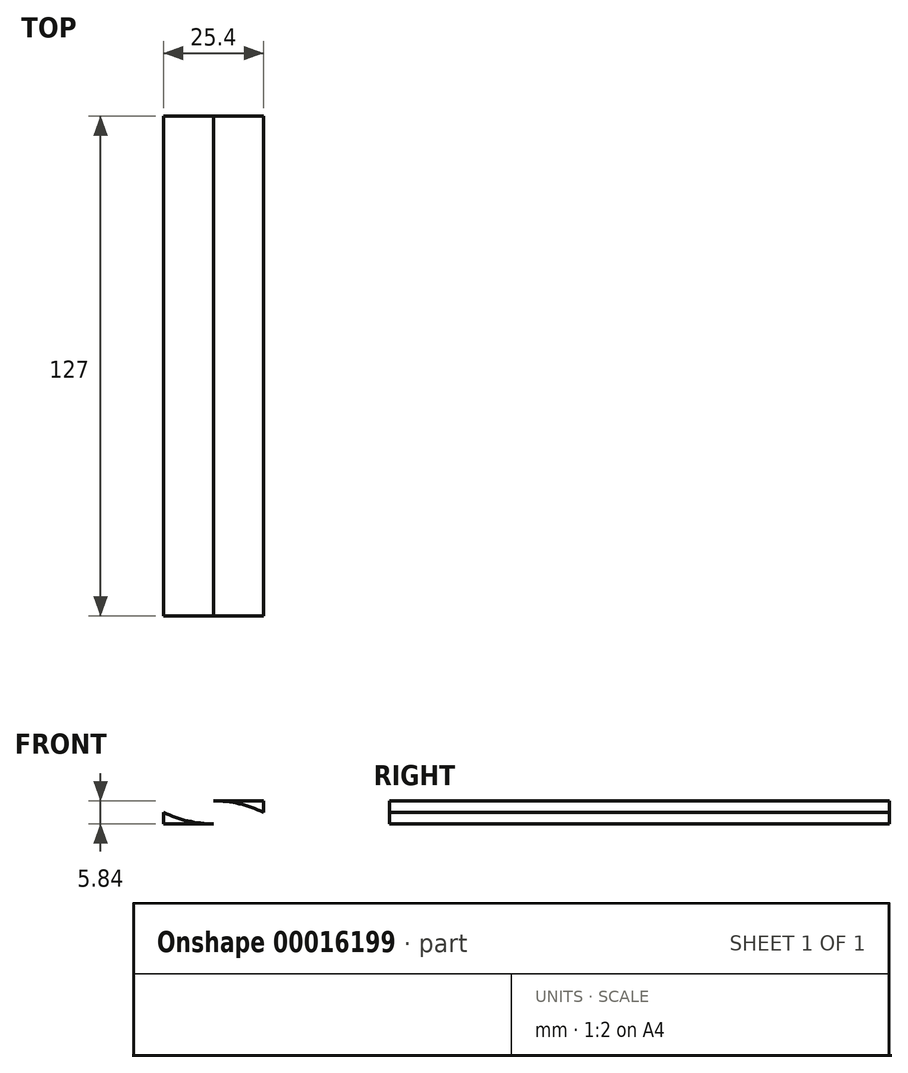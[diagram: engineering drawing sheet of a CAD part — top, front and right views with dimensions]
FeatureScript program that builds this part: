
annotation { "Feature Type Name" : "Feature", "Feature Type Description" : "" }
export const myFeature = defineFeature(function(context is Context, id is Id, definition is map)
    precondition{}
    {
        {
            var Q0;
            Q0=qCreatedBy(makeId("Top.planeOp"),FACE);
            var sketch = newSketch(context, id + "F0", { "sketchPlane" : qUnion([Q0])});
            skLineSegment(sketch, "E0.rect.bottom", {"start": v(-12.7, 63.5) * mm, "end": v(12.7, 63.5) * mm});
            skLineSegment(sketch, "E0.rect.top", {"start": v(-12.7, -63.5) * mm, "end": v(12.7, -63.5) * mm});
            skLineSegment(sketch, "E0.rect.left", {"start": v(-12.7, 63.5) * mm, "end": v(-12.7, -63.5) * mm});
            skLineSegment(sketch, "E0.rect.right", {"start": v(12.7, 63.5) * mm, "end": v(12.7, -63.5) * mm});
            skPoint(sketch, "E0.rect.middle", {"position": v(0, 0) * mm});
            skSolve(sketch);
        }
        {
            var Q0;
            Q0=makeQuery(id+"F0.imprint","IMPRINT",FACE,{"disambiguationData":[TD([[makeQuery(id+"F0.imprint","IMPRINT",EDGE,{"derivedFrom":sQuery(id+"F0.wireOp",EDGE,"E0.rect.bottom")}),-1.0]])]});
            extrude(context, id + "F1", {"entities" : qUnion([Q0]), "endBound" : BoundingType.SYMMETRIC, "depth" : 5.84 * mm});
        }
        {
            var Q0;
            Q0=makeQuery(id+"F1.opExtrude","SWEPT_FACE",FACE,{"disambiguationData":[OSD([sQuery(id+"F0.wireOp",EDGE,"E0.rect.top")])]});
            var sketch = newSketch(context, id + "F2", { "sketchPlane" : qUnion([Q0])});
            skArc(sketch, "E1", {"start": v(0, 2.92) * mm, "mid": v(-6.52, 2.18) * mm, "end": v(-12.7, 0) * mm});
            skLineSegment(sketch, "E2", {"start": v(-12.7, 0) * mm, "end": v(12.7, 0) * mm, "construction": true});
            skLineSegment(sketch, "E3", {"start": v(0, 2.92) * mm, "end": v(0, -2.92) * mm, "construction": true});
            skArc(sketch, "E4.MirrorCS", {"start": v(0, -2.92) * mm, "mid": v(-6.52, -2.18) * mm, "end": v(-12.7, 0) * mm});
            skArc(sketch, "E5.MirrorCS", {"start": v(0, -2.92) * mm, "mid": v(6.52, -2.18) * mm, "end": v(12.7, 0) * mm});
            skArc(sketch, "E6.MirrorCS", {"start": v(0, 2.92) * mm, "mid": v(6.52, 2.18) * mm, "end": v(12.7, 0) * mm});
            skArc(sketch, "E7", {"start": v(-6.52, 2.18) * mm, "mid": v(-8.25, 0) * mm, "end": v(-6.52, -2.18) * mm});
            skArc(sketch, "E8.MirrorCS", {"start": v(6.52, 2.18) * mm, "mid": v(8.25, 0) * mm, "end": v(6.52, -2.18) * mm});
            skSolve(sketch);
        }
        {
            var Q0;
            {var subQ2=sQuery(id+"F2.wireOp",EDGE,"E1");var subQ7=makeQuery(id+"F2.imprint","INTERSECT",VERTEX,{"derivedFrom":[subQ2,sQuery(id+"F2.wireOp",EDGE,"E7")]});Q0=makeQuery(id+"F2.imprint","IMPRINT",FACE,{"disambiguationData":[TD([[makeQuery(id+"F2.imprint","IMPRINT",EDGE,{"disambiguationData":[TD([[subQ7,1.0]])],"derivedFrom":subQ2}),-1.0]])]});}
            var Q1;
            {var subQ0=sQuery(id+"F2.wireOp",EDGE,"E7");Q1=makeQuery(id+"F2.imprint","IMPRINT",FACE,{"disambiguationData":[TD([[makeQuery(id+"F2.imprint","IMPRINT",EDGE,{"derivedFrom":subQ0}),-1.0]])]});}
            var Q2;
            {var subQ2=sQuery(id+"F2.wireOp",EDGE,"E4.MirrorCS");var subQ7=makeQuery(id+"F2.imprint","INTERSECT",VERTEX,{"derivedFrom":[subQ2,sQuery(id+"F2.wireOp",EDGE,"E7")]});Q2=makeQuery(id+"F2.imprint","IMPRINT",FACE,{"disambiguationData":[TD([[makeQuery(id+"F2.imprint","IMPRINT",EDGE,{"disambiguationData":[TD([[subQ7,1.0]])],"derivedFrom":subQ2}),1.0]])]});}
            var Q3;
            {var subQ2=sQuery(id+"F2.wireOp",EDGE,"E6.MirrorCS");var subQ7=makeQuery(id+"F2.imprint","INTERSECT",VERTEX,{"derivedFrom":[subQ2,sQuery(id+"F2.wireOp",EDGE,"E8.MirrorCS")]});Q3=makeQuery(id+"F2.imprint","IMPRINT",FACE,{"disambiguationData":[TD([[makeQuery(id+"F2.imprint","IMPRINT",EDGE,{"disambiguationData":[TD([[subQ7,1.0]])],"derivedFrom":subQ2}),1.0]])]});}
            var Q4;
            {var subQ0=sQuery(id+"F2.wireOp",EDGE,"E8.MirrorCS");Q4=makeQuery(id+"F2.imprint","IMPRINT",FACE,{"disambiguationData":[TD([[makeQuery(id+"F2.imprint","IMPRINT",EDGE,{"derivedFrom":subQ0}),1.0]])]});}
            var Q5;
            {var subQ2=sQuery(id+"F2.wireOp",EDGE,"E5.MirrorCS");var subQ7=makeQuery(id+"F2.imprint","INTERSECT",VERTEX,{"derivedFrom":[subQ2,sQuery(id+"F2.wireOp",EDGE,"E8.MirrorCS")]});Q5=makeQuery(id+"F2.imprint","IMPRINT",FACE,{"disambiguationData":[TD([[makeQuery(id+"F2.imprint","IMPRINT",EDGE,{"disambiguationData":[TD([[subQ7,1.0]])],"derivedFrom":subQ2}),-1.0]])]});}
            extrude(context, id + "F3", {"entities" : qUnion([Q0, Q1, Q2, Q3, Q4, Q5]), "operationType" : NewBodyOperationType.REMOVE, "oppositeDirection" : true, "depth" : 152.4 * mm});
        }
        {
            var Q0;
            Q0=makeQuery(id+"F1.opExtrude","SWEPT_FACE",FACE,{"disambiguationData":[OSD([sQuery(id+"F0.wireOp",EDGE,"E0.rect.top")])]});
            var sketch = newSketch(context, id + "F4", { "sketchPlane" : qUnion([Q0])});
            skLineSegment(sketch, "E9.rect.bottom", {"start": v(-6.35, 1.59) * mm, "end": v(6.35, 1.59) * mm});
            skLineSegment(sketch, "E9.rect.top", {"start": v(-6.35, -1.59) * mm, "end": v(6.35, -1.59) * mm});
            skLineSegment(sketch, "E9.rect.left", {"start": v(-6.35, 1.59) * mm, "end": v(-6.35, -1.59) * mm});
            skLineSegment(sketch, "E9.rect.right", {"start": v(6.35, 1.59) * mm, "end": v(6.35, -1.59) * mm});
            skPoint(sketch, "E9.rect.middle", {"position": v(0, 0) * mm});
            skSolve(sketch);
        }
        {
            var Q0;
            Q0=makeQuery(id+"F4.imprint","IMPRINT",FACE,{"disambiguationData":[TD([[makeQuery(id+"F4.imprint","IMPRINT",EDGE,{"derivedFrom":sQuery(id+"F4.wireOp",EDGE,"E9.rect.bottom")}),-1.0]])]});
            extrude(context, id + "F5", {"entities" : qUnion([Q0]), "operationType" : NewBodyOperationType.REMOVE, "oppositeDirection" : true, "depth" : 127 * mm});
        }
    });
